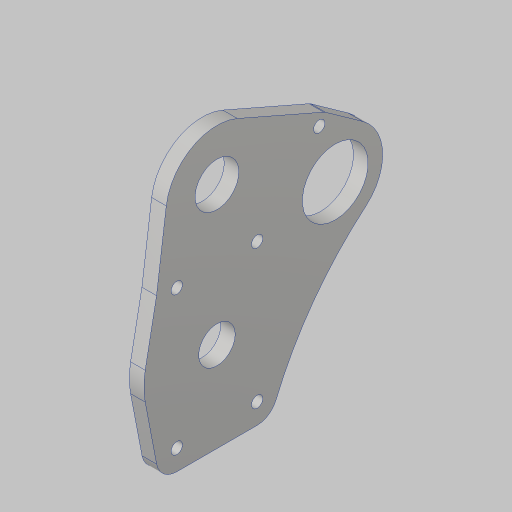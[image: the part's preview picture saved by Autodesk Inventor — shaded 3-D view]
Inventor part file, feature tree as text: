
AUTODESK INVENTOR PART (.ipt)
format: ipt  version: 2023.5 (Build 275446000, 446)  size: 194,048 bytes
history: native  units: in
note: dims shown in document units (in); Inventor stores cm internally (conversion verified against a paired STEP export)
features: sketch x3, extrude x2, hole x1
ambient origin geometry x8: Origin, YZ Plane, XZ Plane, XY Plane, X Axis, Y Axis, Z Axis, Center Point
bodies: Solid1 (feature_tree)
feature tree (6):
  sketch  "Sketch1"  dims[d0=3.0in d1=2.2in]
  sketch  "Sketch2"  dims[d2=3.0in d3=2.375in]
  extrude  "Extrusion1"  Depth=2.2in
  hole  "Hole3"  [1 undecoded]
  extrude  "Extrusion5"  Depth=0.25in
  sketch  "Sketch6"  dims[d4=1.375in d5=0.201in d6=0.201in d7=0.201in d8=0.201in d9=1.0in d12=2.3622in d14=360.0deg d16=1.125in d17=2.246in d19=2.5in d20=0.75in d23=0.25in d24=0.25in d25=0.0in d41=1.1811in d43=360.0deg d45=0.375in d46=0.385in d47=0.375in d49=0.196in d50=0.75in d51=0.385in d52=0.25in d53=0.5635in d54=1.0in d55=0.8108in d56=2.0in d57=0.25in d58=1.75in d60=3.0in d65=2.362in d66=0.25in d75=0.6in d76=2.0in d77=1.75in d78=0.875in d79=5.5in d80=0.625in d81=0.25in d82=0.0in]
note: 1 required parameter value undecoded (feature->parameter linkage not recoverable at this tier; creation-order binding heuristic only, values carry confidence <= 0.55)
